# Revit family: Basisschutz für 4-adrige informationstechnische Systeme mit RJ45
name_source: partatom
category: Generic Models
revit_build: Autodesk Revit 2015 (Build: 20140606_1530(x64)
units: mm (PartAtom-declared; Revit-internal decimal feet)

## types (3) — shared parameters
Height = 38 mm  [stored 0.124672 ft]
Length = 103 mm  [stored 0.337927 ft]
Length 1 = 218 mm  [stored 0.715223 ft]
Manufacturer = OBO Bettermann
Material = Aluminum
URL = http://www.obo-bettermann.com
Width = 28 mm  [stored 0.0918635 ft]

## per-type parameters (varying)
| type | GTIN | Manufacturer Art.No. |
| RJ45 S-E100 4-B | 4012196415748 | 5081001 |
| RJ45 S-E100 4-C | 4012196415755 | 5081003 |
| RJ45 S-E100 4-F | 4012196415762 | 5081005 |

note: column(s) folded — value = type name in every type: Article Type

note: [stored X ft] marks values corroborated as IEEE doubles in the binary element streams (Revit-internal decimal feet)

## geometry (parser evidence)
native form markers: Sweep x2
no freeform markers — native parametric forms only
